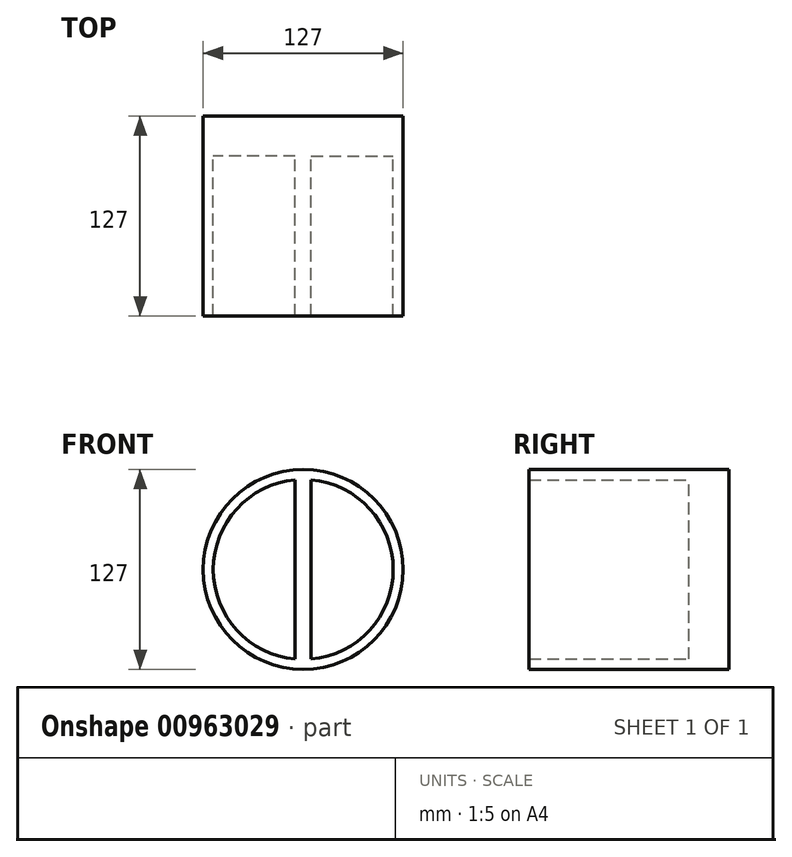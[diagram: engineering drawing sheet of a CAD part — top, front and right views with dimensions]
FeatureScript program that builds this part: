
annotation { "Feature Type Name" : "Feature", "Feature Type Description" : "" }
export const myFeature = defineFeature(function(context is Context, id is Id, definition is map)
    precondition{}
    {
        {
            var Q0;
            Q0=qCreatedBy(makeId("Front.planeOp"),FACE);
            var sketch = newSketch(context, id + "F0", { "sketchPlane" : qUnion([Q0])});
            skCircle(sketch, "E0", {"center": v(0, 0) * mm, "radius": 63.5 * mm});
            skSolve(sketch);
        }
        {
            var Q0;
            Q0 = qSketchRegion(id + "F0", true);
            var Q1;
            Q1 = qSketchRegion(id + "F2", true);
            extrude(context, id + "F1", {"entities" : qUnion([Q0, Q1]), "depth" : 127 * mm, "offsetDistance" : 25.4 * mm});
        }
        {
            var Q0;
            Q0=makeQuery(id+"F1.opExtrude","CAP_FACE",FACE,{"disambiguationData":[OSD([sQuery(id+"F0.wireOp",EDGE,"E0")])],"isStart":true});
            var sketch = newSketch(context, id + "F2", { "sketchPlane" : qUnion([Q0])});
            skSolve(sketch);
        }
        {
            var Q0;
            Q0=makeQuery(id+"F2.imprint","IMPRINT",FACE,{"disambiguationData":[TD([[makeQuery(id+"F2.imprint","IMPRINT",EDGE,{"derivedFrom":makeQuery(id+"F1.opExtrude","CAP_EDGE",EDGE,{"disambiguationData":[OSD([sQuery(id+"F0.wireOp",EDGE,"E0")])],"isStart":true})}),-1.0]])]});
            var sketch = newSketch(context, id + "F3", { "sketchPlane" : qUnion([Q0])});
            skCircle(sketch, "E1", {"center": v(0, 0) * mm, "radius": 57.15 * mm});
            skSolve(sketch);
        }
        {
            var Q0;
            Q0=sQuery(id+"F3.wireOp",VERTEX,"E1.center");
            var Q1;
            Q1=makeQuery(id+"F1.opExtrude","SWEPT_BODY",BODY,{"disambiguationData":[OSD([sQuery(id+"F0.wireOp",EDGE,"E0")])]});
            hole(context, id + "F4", {"style" : HoleStyle.SIMPLE, "endStyle" : HoleEndStyle.THROUGH, "holeDiameter" : 114.3 * mm, "majorDiameter" : 6.35 * mm, "isTappedThrough" : true, "tappedDepth" : 12.7 * mm, "tapClearance" : 3, "locations" : qUnion([Q0]), "scope" : qUnion([Q1])});
        }
        {
            var Q0;
            Q0 = qSketchRegion(id + "F0", true);
            extrude(context, id + "F5", {"entities" : qUnion([Q0]), "operationType" : NewBodyOperationType.ADD, "depth" : 25.4 * mm, "offsetDistance" : 25.4 * mm});
        }
        {
            var Q0;
            Q0=makeQuery(id+"F5.opExtrude","CAP_FACE",FACE,{"disambiguationData":[OSD([sQuery(id+"F0.wireOp",EDGE,"E0")])],"isStart":false});
            var sketch = newSketch(context, id + "F6", { "sketchPlane" : qUnion([Q0])});
            skPoint(sketch, "E2.middle", {"position": v(0, 0) * mm});
            skLineSegment(sketch, "E3.bottom", {"start": v(-5.06, -60.4) * mm, "end": v(5.06, -60.4) * mm});
            skLineSegment(sketch, "E3.top", {"start": v(-5.06, 60.4) * mm, "end": v(5.06, 60.4) * mm});
            skLineSegment(sketch, "E3.left", {"start": v(-5.06, -60.4) * mm, "end": v(-5.06, 60.4) * mm});
            skLineSegment(sketch, "E3.right", {"start": v(5.06, -60.4) * mm, "end": v(5.06, 60.4) * mm});
            skSolve(sketch);
        }
        {
            var Q0;
            Q0 = qSketchRegion(id + "F6", true);
            extrude(context, id + "F7", {"entities" : qUnion([Q0]), "operationType" : NewBodyOperationType.ADD, "depth" : 101.6 * mm, "offsetDistance" : 25.4 * mm});
        }
    });
